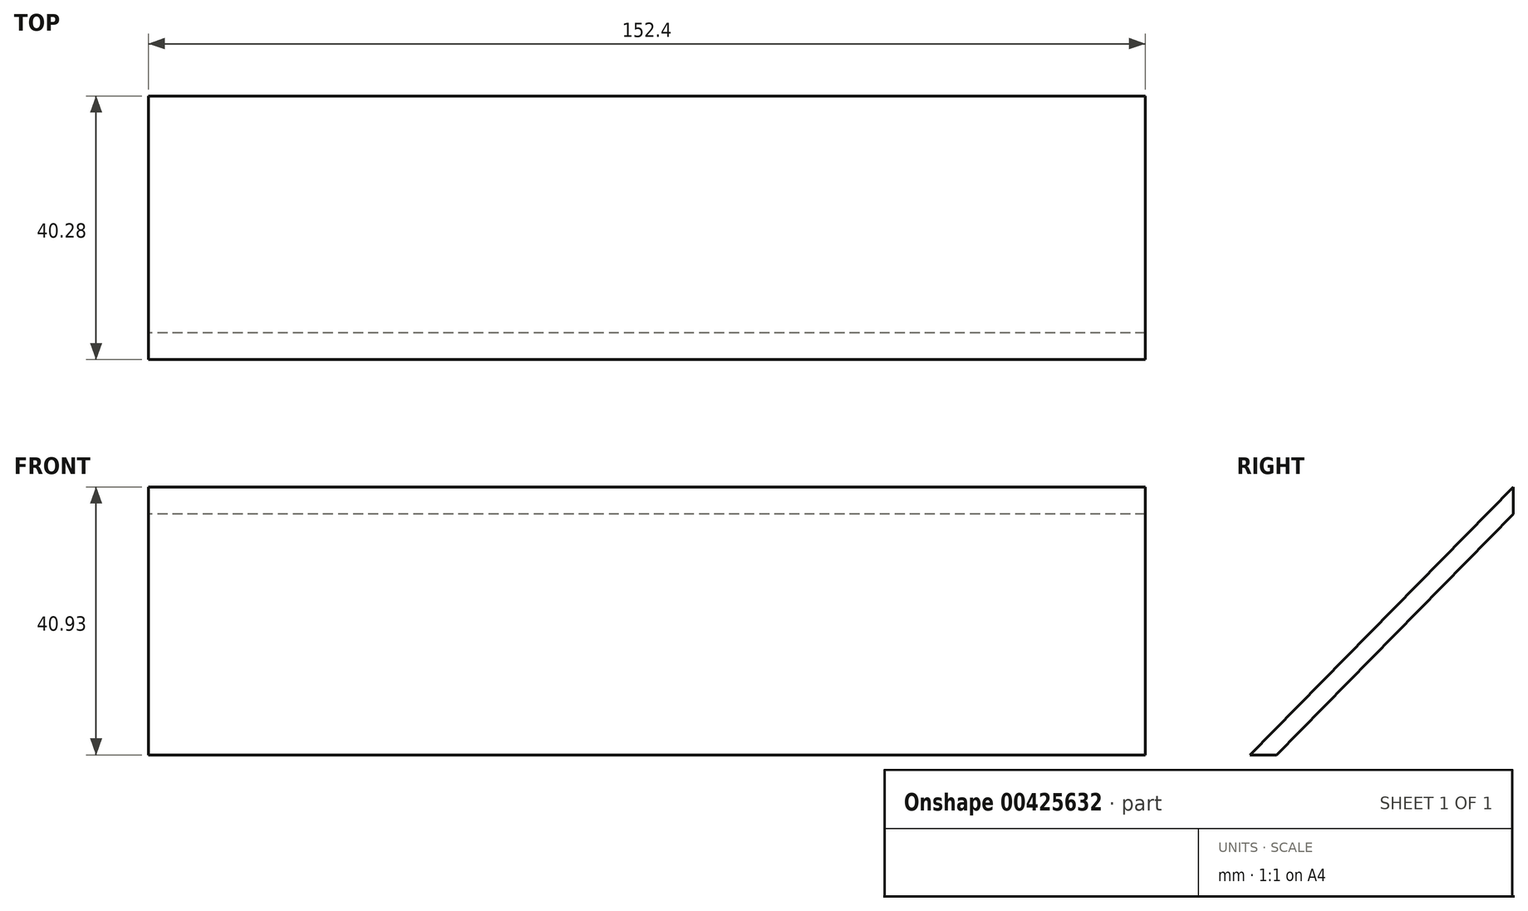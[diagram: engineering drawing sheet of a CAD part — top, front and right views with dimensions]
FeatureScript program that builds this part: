
annotation { "Feature Type Name" : "Feature", "Feature Type Description" : "" }
export const myFeature = defineFeature(function(context is Context, id is Id, definition is map)
    precondition{}
    {
        {
            var Q0;
            Q0=qCreatedBy(makeId("Right.planeOp"),FACE);
            var sketch = newSketch(context, id + "F0", { "sketchPlane" : qUnion([Q0])});
            skLineSegment(sketch, "E0", {"start": v(0, 40.93) * mm, "end": v(-40.28, 0) * mm});
            skLineSegment(sketch, "E1", {"start": v(-40.28, 0) * mm, "end": v(-36.24, 0) * mm});
            skLineSegment(sketch, "E2", {"start": v(-36.24, 0) * mm, "end": v(0, 36.82) * mm});
            skLineSegment(sketch, "E3", {"start": v(0, 36.82) * mm, "end": v(0, 40.93) * mm});
            skSolve(sketch);
        }
        {
            var Q0;
            Q0=makeQuery(id+"F0.imprint","IMPRINT",FACE,{"disambiguationData":[TD([[makeQuery(id+"F0.imprint","IMPRINT",EDGE,{"derivedFrom":sQuery(id+"F0.wireOp",EDGE,"E0")}),1.0]])]});
            extrude(context, id + "F1", {"entities" : qUnion([Q0]), "depth" : 152.4 * mm});
        }
    });
